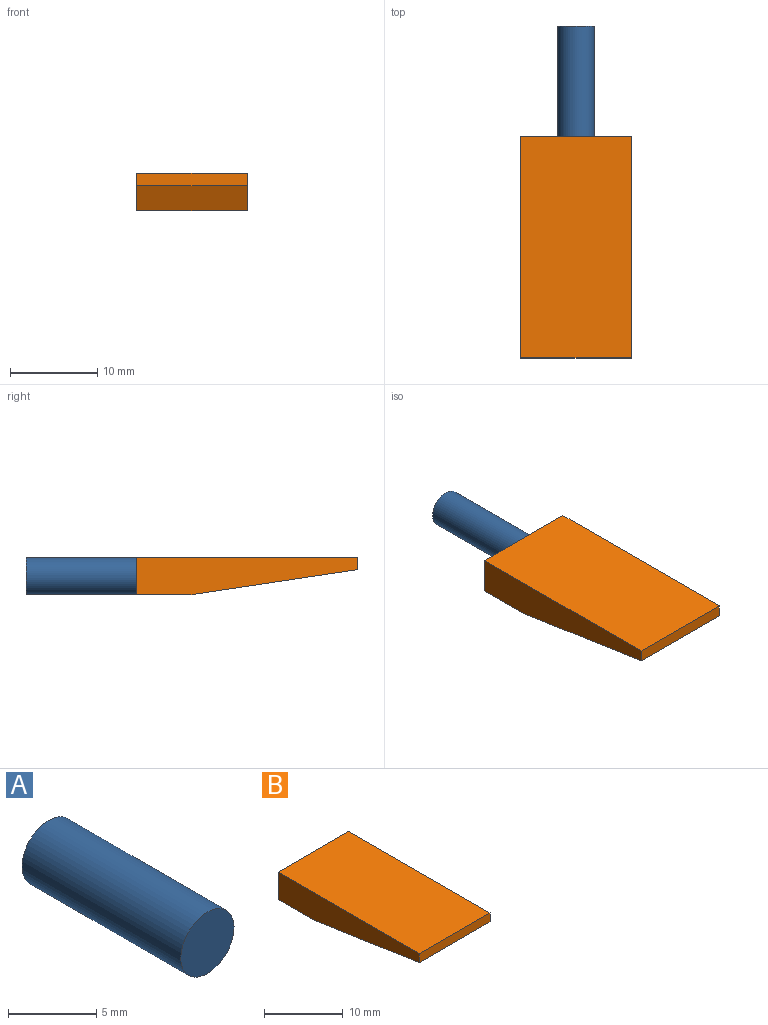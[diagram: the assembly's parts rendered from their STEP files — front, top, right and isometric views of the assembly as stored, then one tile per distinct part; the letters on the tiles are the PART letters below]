
ASSEMBLY  parts=2 mates=1
PART A: 3 faces, bbox 4.3x12.7x4.3 mm
  f0: cylinder r=2.12mm len=12.7mm, axis (0,1,0), area 169.6mm2, adj f1,f2
  f1: plane 4.25x4.25mm, normal (0,-1,0), area 14.2mm2, adj f0
  f2: plane 4.25x4.25mm, normal (0,1,0), area 14.2mm2, adj f0
PART B: 7 faces, bbox 12.7x25.4x4.3 mm
  f0: plane 25.4x4.25mm, normal (1,0,0), area 80.7mm2, adj f1,f3,f4,f5,f6
  f1: plane 25.4x12.7mm, normal (0,0,1), area 322.6mm2, adj f0,f2,f4,f5
  f2: plane 25.4x4.25mm, normal (-1,0,0), area 80.7mm2, adj f1,f3,f4,f5,f6
  f3: plane 12.7x6.35mm, normal (0,0,-1), area 80.6mm2, adj f0,f2,f5,f6
  f4: plane 12.7x1.39mm, normal (0,-1,0), area 17.7mm2, adj f0,f1,f2,f6
  f5: plane 12.7x4.25mm, normal (0,1,0), area 54mm2, adj f0,f1,f2,f3
  f6: plane 19.05x12.7mm, normal (0,-0.15,-0.99), area 244.6mm2, adj f0,f2,f3,f4
PLACE A t=(-1.19,23.4,-1.98)mm
PLACE B t=(-6.99,10.7,-1.24)mm
MATE fastened A.f0 <-> B.f5  axis (0,-1,0) through (-1.19,10.7,-1.98)mm
